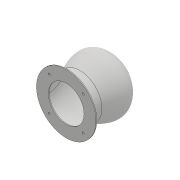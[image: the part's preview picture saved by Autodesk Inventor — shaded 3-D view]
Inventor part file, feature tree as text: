
AUTODESK INVENTOR PART (.ipt)
format: ipt  version: 2018 (Build 220112000, 112)  size: 355,328 bytes
history: native  units: mm
features: sketch x5, extrude x2, hole x2, revolve x1, shell x1, fillet x1, projected_geometry x1
ambient origin geometry x8: Origin, YZ Plane, XZ Plane, XY Plane, X Axis, Y Axis, Z Axis, Center Point
bodies: Solid1 (feature_tree)
feature tree (13):
  revolve  "Revolution1"  [1 undecoded]
  sketch  "Sketch2"  dims[d3=21.0mm d4=28.0mm]
  shell  "Shell1"  Thickness=38.0mm
  extrude  "Extrusion3"  Depth=28.0mm
  hole  "Hole2"  [1 undecoded]
  extrude  "Extrusion2"  Depth=12.5mm
  fillet  "Fillet2"  Radius=21.0mm
  hole  "Hole4"  [1 undecoded]
  sketch  "Sketch1"  dims[d0=55.0mm d1=33.0mm d2=38.0mm]
  sketch  "Sketch5"  dims[d5=20.0mm d6=22.0mm]
  sketch  "Sketch6"  dims[d7=90.0deg d8=12.5mm d9=21.0mm]
  sketch  "Sketch8"  dims[d10=6.5mm d11=1.0mm d26=1.567mm d27=4.0mm d28=6.3mm d29=2.0mm d30=90.0deg d31=6.3mm d32=20.594885mm d33=12.0mm d34=1.0mm d35=0.0mm d36=70.0mm d37=1.0mm d38=0.0mm d48=11.0mm d49=40.0mm d50=40.0mm d51=2.459mm d52=6.0mm d53=6.3mm d54=2.0mm d55=90.0deg d56=8.8mm d57=20.594885mm]
  projected_geometry  "Project Cut Edges2"
note: 3 required parameter values undecoded (feature->parameter linkage not recoverable at this tier; creation-order binding heuristic only, values carry confidence <= 0.55)